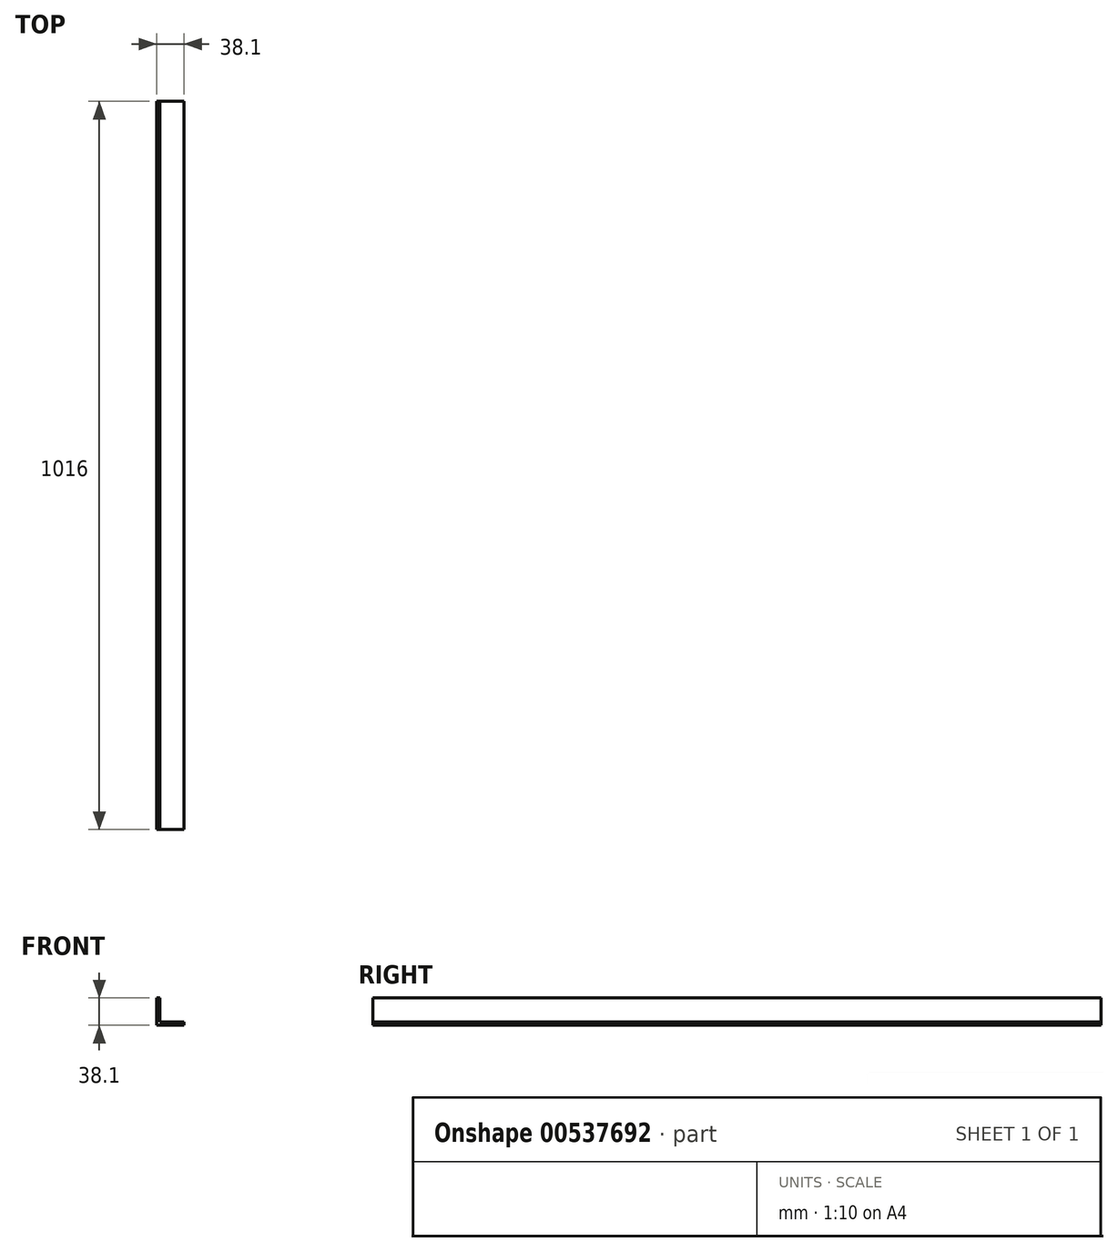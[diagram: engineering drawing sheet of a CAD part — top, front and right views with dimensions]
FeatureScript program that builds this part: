
annotation { "Feature Type Name" : "Feature", "Feature Type Description" : "" }
export const myFeature = defineFeature(function(context is Context, id is Id, definition is map)
    precondition{}
    {
        {
            var Q0;
            Q0=qCreatedBy(makeId("Front.planeOp"),FACE);
            var sketch = newSketch(context, id + "F0", { "sketchPlane" : qUnion([Q0])});
            skLineSegment(sketch, "E0", {"start": v(0, 0) * mm, "end": v(0, 38.1) * mm});
            skLineSegment(sketch, "E1", {"start": v(0, 38.1) * mm, "end": v(4.76, 38.1) * mm});
            skLineSegment(sketch, "E2", {"start": v(4.76, 38.1) * mm, "end": v(4.76, 4.76) * mm});
            skLineSegment(sketch, "E3", {"start": v(4.76, 4.76) * mm, "end": v(38.1, 4.76) * mm});
            skLineSegment(sketch, "E4", {"start": v(38.1, 4.76) * mm, "end": v(38.1, 0) * mm});
            skLineSegment(sketch, "E5", {"start": v(38.1, 0) * mm, "end": v(0, 0) * mm});
            skSolve(sketch);
        }
        {
            var Q0;
            Q0 = qSketchRegion(id + "F0", true);
            extrude(context, id + "F1", {"entities" : qUnion([Q0]), "oppositeDirection" : true, "depth" : 1016 * mm, "offsetDistance" : 25.4 * mm});
        }
    });
